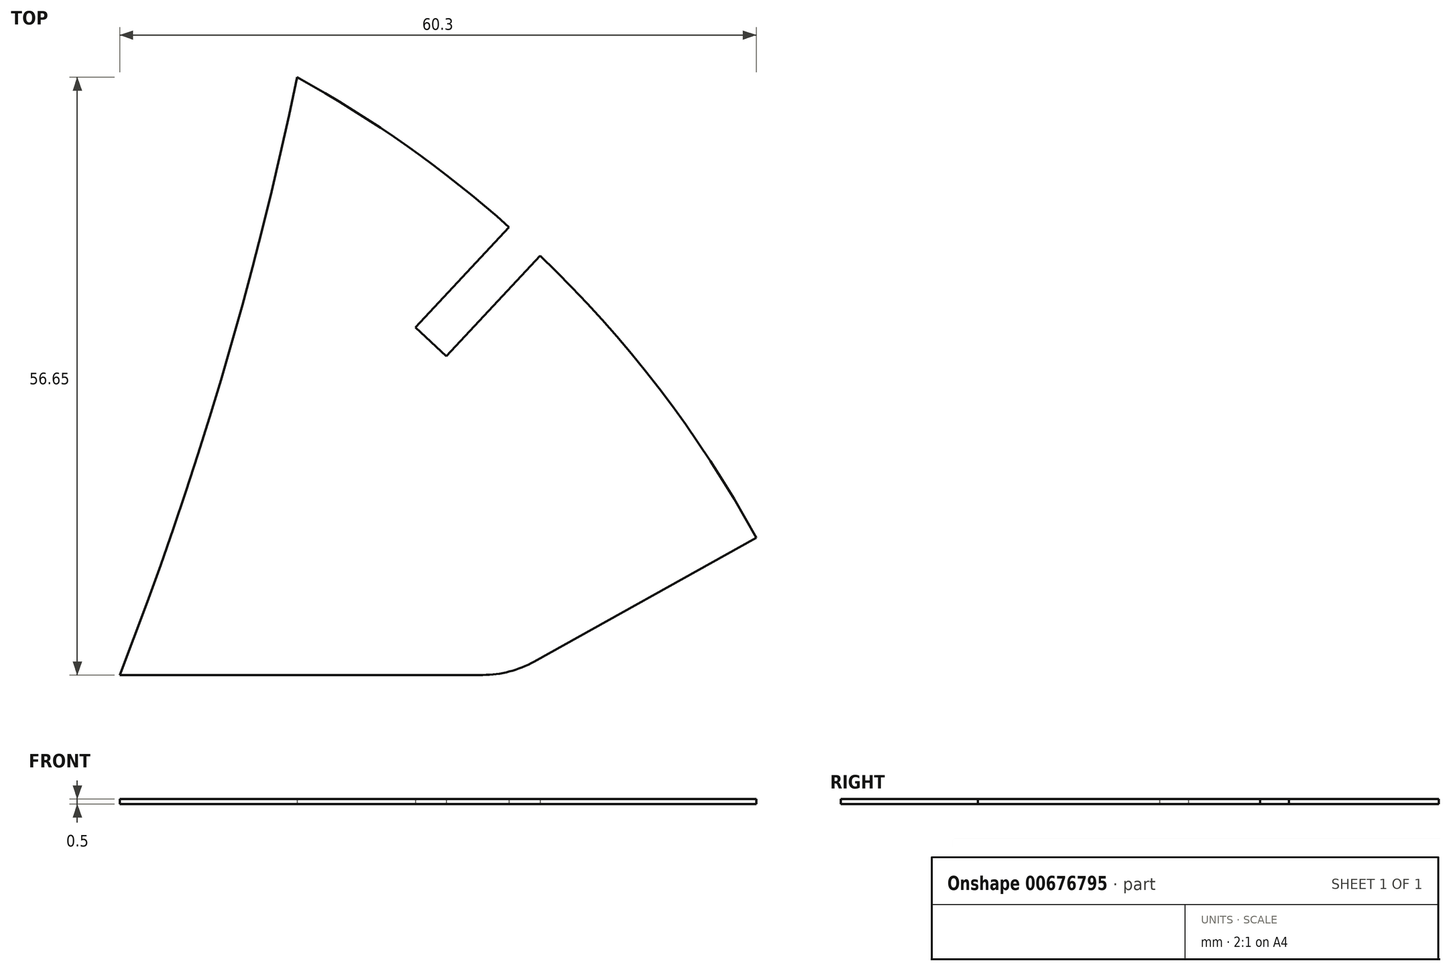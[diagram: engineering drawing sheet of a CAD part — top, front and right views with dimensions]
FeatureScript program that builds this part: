
annotation { "Feature Type Name" : "Feature", "Feature Type Description" : "" }
export const myFeature = defineFeature(function(context is Context, id is Id, definition is map)
    precondition{}
    {
        {
            var Q0;
            Q0=qCreatedBy(makeId("Top.planeOp"),FACE);
            var sketch = newSketch(context, id + "F0", { "sketchPlane" : qUnion([Q0])});
            skArc(sketch, "E0", {"start": v(24.47, 51.93) * mm, "mid": v(48.48, 30.75) * mm, "end": v(57.4, 0) * mm, "construction": true});
            skLineSegment(sketch, "E1", {"start": v(24.47, 51.93) * mm, "end": v(0, 0) * mm, "construction": true});
            skLineSegment(sketch, "E2", {"start": v(37, 0) * mm, "end": v(60.3, 13) * mm});
            skLineSegment(sketch, "E3", {"start": v(9, 23) * mm, "end": v(16.8, 56.65) * mm, "construction": true});
            skArc(sketch, "E4", {"start": v(60.3, 13) * mm, "mid": v(51.1, 27.16) * mm, "end": v(39.83, 39.74) * mm});
            skLineSegment(sketch, "E5", {"start": v(9, 23) * mm, "end": v(0, 0) * mm, "construction": true});
            skLineSegment(sketch, "E6", {"start": v(0, 0) * mm, "end": v(37, 0) * mm});
            skLineSegment(sketch, "E7", {"start": v(38.37, 41.1) * mm, "end": v(0, 0) * mm, "construction": true});
            skLineSegment(sketch, "E8", {"start": v(36.9, 42.45) * mm, "end": v(28.02, 32.95) * mm});
            skLineSegment(sketch, "E9", {"start": v(28.02, 32.95) * mm, "end": v(30.94, 30.22) * mm});
            skLineSegment(sketch, "E10", {"start": v(30.94, 30.22) * mm, "end": v(39.83, 39.74) * mm});
            skArc(sketch, "E11", {"start": v(36.9, 42.45) * mm, "mid": v(27.24, 50.11) * mm, "end": v(16.8, 56.65) * mm});
            skArc(sketch, "E12", {"start": v(39.83, 39.74) * mm, "mid": v(38.37, 41.1) * mm, "end": v(36.9, 42.45) * mm, "construction": true});
            skArc(sketch, "E13", {"start": v(0, 0) * mm, "mid": v(9.6, 27.97) * mm, "end": v(16.8, 56.65) * mm});
            skSolve(sketch);
        }
        {
            var Q0;
            Q0 = qSketchRegion(id + "F0", true);
            extrude(context, id + "F1", {"entities" : qUnion([Q0]), "depth" : 0.5 * mm, "offsetDistance" : 25 * mm});
        }
        {
            var Q0;
            Q0=makeQuery(id+"F1.opExtrude","SWEPT_EDGE",EDGE,{"disambiguationData":[OSD([sQuery(id+"F0.wireOp",EDGE,"E2"),sQuery(id+"F0.wireOp",EDGE,"E6")])]});
            fillet(context, id + "F2", {"entities" : qUnion([Q0]), "radius" : 10 * mm, "tangentPropagation" : true, "allowEdgeOverflow" : false});
        }
    });
